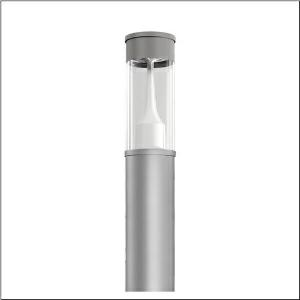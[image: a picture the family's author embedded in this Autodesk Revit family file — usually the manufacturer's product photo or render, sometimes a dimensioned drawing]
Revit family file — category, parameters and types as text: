
# Revit family: city-light_400_iq___p1_0a_5xa5305lf14hp_1a81
name_source: partatom
category: Lighting Fixtures
units: mm (PartAtom-declared; Revit-internal decimal feet)

## family parameters
Cut with Voids When Loaded = No
Host = Face
Light Source = No
Part Type = Normal
Room Calculation Point = No
Round Connector Dimension = Use Diameter
Shared = No

## types (1)
- --- (1 x LED, 4910 lm, 33.6 W, 4000K)
    Apparent Load = 34 VA
    CIE Flux Codes = 31 62 91 95 100
    Color Rendering = 70
    Color Temperature = 4000K
    Default Elevation = 1800 mm
    Description = City-Light 400 iQ, light pillar, Module 540 iQ-SR, primary light control with 3 zone facetted reflector, of plastic, silver coated, highly specular, structured, primary optical cover: cover, of PMMA, transparent, partly coated, light distribution: P1.0a, primary light characteristic: strongly asymmetric, LED, High Power LED, rated luminous flux: 4.910lm, luminous efficacy: 146lm/W, light colour: 740, colour temperature: 4000K, control gear: ECG iQ, control: pre-setting: logarithmic dimming characteristic, Street-Remote, Auto-Match, Temp-Guard, Lumen-Switch, Night-Set, Smart-Wire, Light-Fading, Desk-Remote (wireless, voltage-free reading and setting of iQ features in the workshop via application-optimized NFC function/RFID function), optimised constant luminous flux control (CLO 2.0), with terminal, 6-pole, max. 2.5mm², mains connection: 230..240V, AC, 50/60Hz, start of lifetime: 34W, end of service life: 36W, reduction: 15W, luminaire housing, cylindrical, of extruded aluminium section, coated, Siteco® metallic grey (DB 702S), length: 4.694mm, diameter: 200mm, Module 540 iQ-SR, traffic white (RAL 9016), equipment: Power, protection rating (complete): IP65, insulation class (complete): insulation class II (safety insulation), certification: CE, ENEC, VDE, packaging unit: 1 piece

Light Distribution: P1.0a
    Height = 500 mm
    Lamp = 1 x LED
    Lamp Light Flux = 4910 lm
    Lamp Power = 33.6 W
    Lamp count = 1
    Length = 200 mm  [stored 0.656168 ft]
    Luminous efficacy = 146 lm/W
    Manufacturer = Siteco
    ModVariant = No
    Model = 5XA5305LF14HP
    Mounting Place = Floor
    Mounting Type = Freestanding
    Number of Poles = 1
    OnlyDefault = Yes
    Power Factor = 1
    Product Name = City-Light 400 iQ | P1.0a
    Product group = light pillar
    ProductGroupID = 1301
    Protection Class = Protection class II
    Protection Degree = IP 65
    RLX_Detail_Level = 1
    RLX_Emergency_Light_Flux = 0 lm
    RLX_Emergency_Type = 0
    RLX_Emergency_Type_DB = No
    RlxData = <blob elided: 53557 chars, md5=fea20421>
    Socket = socket
    Standby Power = 0 W
    System Light Flux = 4910 lm
    System Power = 34 W
    Type Comments = factory setting: luminous flux: 100 % | dim-lin: 254 | 695 mA
    Type Image = l_1006916.jpg
    URL = http://relux.com
    VarID = @adj_165393
    Voltage = 0 V
    Weight = 0.00 kg
    Width = 0 mm  [stored 0 ft]

note: [stored X ft] marks values corroborated as IEEE doubles in the binary element streams (Revit-internal decimal feet)

## geometry (parser evidence)
native form markers: Blend x4, Sweep x13
no freeform markers — native parametric forms only
